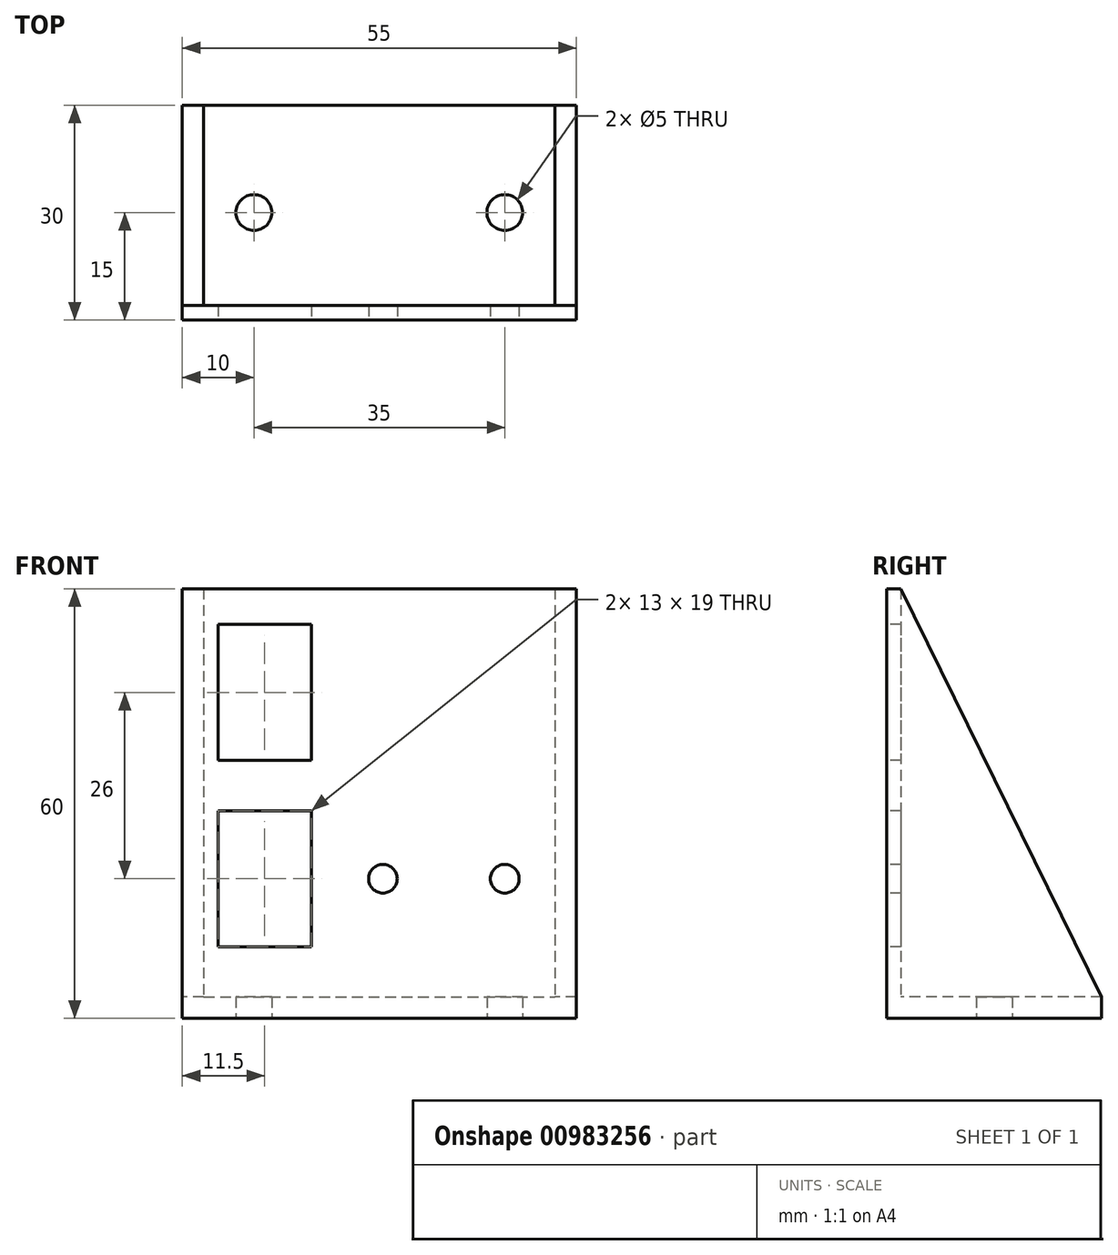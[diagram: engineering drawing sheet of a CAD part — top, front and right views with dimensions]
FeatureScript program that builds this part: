
annotation { "Feature Type Name" : "Feature", "Feature Type Description" : "" }
export const myFeature = defineFeature(function(context is Context, id is Id, definition is map)
    precondition{}
    {
        {
            var Q0;
            Q0=qCreatedBy(makeId("Top.planeOp"),FACE);
            var sketch = newSketch(context, id + "F0", { "sketchPlane" : qUnion([Q0])});
            skLineSegment(sketch, "E0.bottom", {"start": v(27.5, 15) * mm, "end": v(-27.5, 15) * mm});
            skLineSegment(sketch, "E0.top", {"start": v(27.5, -15) * mm, "end": v(-27.5, -15) * mm});
            skLineSegment(sketch, "E0.left", {"start": v(27.5, 15) * mm, "end": v(27.5, -15) * mm});
            skLineSegment(sketch, "E0.right", {"start": v(-27.5, 15) * mm, "end": v(-27.5, -15) * mm});
            skPoint(sketch, "E0.middle", {"position": v(0, 0) * mm});
            skLineSegment(sketch, "E1.bottom", {"start": v(-27.5, 15) * mm, "end": v(27.5, 15) * mm, "construction": true});
            skLineSegment(sketch, "E1.top", {"start": v(-27.5, 0) * mm, "end": v(27.5, 0) * mm, "construction": true});
            skLineSegment(sketch, "E1.left", {"start": v(-27.5, 15) * mm, "end": v(-27.5, 0) * mm, "construction": true});
            skLineSegment(sketch, "E1.right", {"start": v(27.5, 15) * mm, "end": v(27.5, 0) * mm, "construction": true});
            skLineSegment(sketch, "E2.bottom", {"start": v(-27.5, -15) * mm, "end": v(-17.5, -15) * mm, "construction": true});
            skLineSegment(sketch, "E2.top", {"start": v(-27.5, 15) * mm, "end": v(-17.5, 15) * mm, "construction": true});
            skLineSegment(sketch, "E2.left", {"start": v(-27.5, -15) * mm, "end": v(-27.5, 15) * mm, "construction": true});
            skLineSegment(sketch, "E2.right", {"start": v(-17.5, -15) * mm, "end": v(-17.5, 15) * mm, "construction": true});
            skLineSegment(sketch, "E3.bottom", {"start": v(27.5, 15) * mm, "end": v(17.5, 15) * mm, "construction": true});
            skLineSegment(sketch, "E3.top", {"start": v(27.5, -15) * mm, "end": v(17.5, -15) * mm, "construction": true});
            skLineSegment(sketch, "E3.left", {"start": v(27.5, 15) * mm, "end": v(27.5, -15) * mm, "construction": true});
            skLineSegment(sketch, "E3.right", {"start": v(17.5, 15) * mm, "end": v(17.5, -15) * mm, "construction": true});
            skCircle(sketch, "E4", {"center": v(-17.5, 0) * mm, "radius": 2.5 * mm});
            skCircle(sketch, "E5", {"center": v(17.5, 0) * mm, "radius": 2.5 * mm});
            skLineSegment(sketch, "E6.bottom", {"start": v(-27.5, 15) * mm, "end": v(-24.5, 15) * mm});
            skLineSegment(sketch, "E6.top", {"start": v(-27.5, -15) * mm, "end": v(-24.5, -15) * mm});
            skLineSegment(sketch, "E6.right", {"start": v(-24.5, 15) * mm, "end": v(-24.5, -15) * mm});
            skLineSegment(sketch, "E7.bottom", {"start": v(27.5, 15) * mm, "end": v(24.5, 15) * mm});
            skLineSegment(sketch, "E7.top", {"start": v(27.5, -15) * mm, "end": v(24.5, -15) * mm});
            skLineSegment(sketch, "E7.right", {"start": v(24.5, 15) * mm, "end": v(24.5, -15) * mm});
            skLineSegment(sketch, "E8.bottom", {"start": v(-27.5, -15) * mm, "end": v(27.5, -15) * mm});
            skLineSegment(sketch, "E8.top", {"start": v(-27.5, -13) * mm, "end": v(27.5, -13) * mm});
            skLineSegment(sketch, "E8.left", {"start": v(-27.5, -15) * mm, "end": v(-27.5, -13) * mm});
            skLineSegment(sketch, "E8.right", {"start": v(27.5, -15) * mm, "end": v(27.5, -13) * mm});
            skSolve(sketch);
        }
        {
            var Q0;
            Q0=makeQuery(id+"F0.imprint","IMPRINT",FACE,{"disambiguationData":[TD([[makeQuery(id+"F0.imprint","IMPRINT",EDGE,{"derivedFrom":sQuery(id+"F0.wireOp",EDGE,"E4")}),-1.0]])]});
            extrude(context, id + "F1", {"entities" : qUnion([Q0]), "depth" : 3 * mm, "offsetDistance" : 25 * mm});
        }
        {
            var Q0;
            {var subQ0=sQuery(id+"F0.wireOp",EDGE,"E0.right");var subQ1=sQuery(id+"F0.wireOp",EDGE,"E0.bottom");var subQ2=makeQuery(id+"F0.imprint","INTERSECT",VERTEX,{"derivedFrom":[subQ1,subQ0]});Q0=makeQuery(id+"F0.imprint","IMPRINT",FACE,{"disambiguationData":[TD([[makeQuery(id+"F0.imprint","IMPRINT",EDGE,{"disambiguationData":[TD([[subQ2,1.0]])],"derivedFrom":subQ1}),1.0]])]});}
            var Q1;
            {var subQ0=sQuery(id+"F0.wireOp",EDGE,"E0.right");var subQ1=sQuery(id+"F0.wireOp",EDGE,"E0.top");var subQ2=makeQuery(id+"F0.imprint","INTERSECT",VERTEX,{"derivedFrom":[subQ1,subQ0]});Q1=makeQuery(id+"F0.imprint","IMPRINT",FACE,{"disambiguationData":[TD([[makeQuery(id+"F0.imprint","IMPRINT",EDGE,{"disambiguationData":[TD([[subQ2,1.0]])],"derivedFrom":subQ1}),-1.0]])]});}
            var Q2;
            {var subQ0=sQuery(id+"F0.wireOp",EDGE,"E7.right");var subQ1=sQuery(id+"F0.wireOp",EDGE,"E0.top");var subQ2=makeQuery(id+"F0.imprint","INTERSECT",VERTEX,{"derivedFrom":[subQ1,subQ0]});Q2=makeQuery(id+"F0.imprint","IMPRINT",FACE,{"disambiguationData":[TD([[makeQuery(id+"F0.imprint","IMPRINT",EDGE,{"disambiguationData":[TD([[subQ2,-1.0]])],"derivedFrom":subQ1}),-1.0]])]});}
            var Q3;
            {var subQ0=sQuery(id+"F0.wireOp",EDGE,"E7.right");var subQ1=sQuery(id+"F0.wireOp",EDGE,"E0.top");var subQ2=makeQuery(id+"F0.imprint","INTERSECT",VERTEX,{"derivedFrom":[subQ1,subQ0]});Q3=makeQuery(id+"F0.imprint","IMPRINT",FACE,{"disambiguationData":[TD([[makeQuery(id+"F0.imprint","IMPRINT",EDGE,{"disambiguationData":[TD([[subQ2,1.0]])],"derivedFrom":subQ1}),-1.0]])]});}
            var Q4;
            {var subQ0=sQuery(id+"F0.wireOp",EDGE,"E7.right");var subQ1=sQuery(id+"F0.wireOp",EDGE,"E0.bottom");var subQ2=makeQuery(id+"F0.imprint","INTERSECT",VERTEX,{"derivedFrom":[subQ1,subQ0]});Q4=makeQuery(id+"F0.imprint","IMPRINT",FACE,{"disambiguationData":[TD([[makeQuery(id+"F0.imprint","IMPRINT",EDGE,{"disambiguationData":[TD([[subQ2,1.0]])],"derivedFrom":subQ1}),1.0]])]});}
            extrude(context, id + "F2", {"entities" : qUnion([Q0, Q1, Q2, Q3, Q4]), "operationType" : NewBodyOperationType.ADD, "depth" : 60 * mm, "offsetDistance" : 25 * mm});
        }
        {
            var Q0;
            Q0=makeQuery(id+"F2.opExtrude","SWEPT_FACE",FACE,{"disambiguationData":[OSD([sQuery(id+"F0.wireOp",EDGE,"E0.right")])]});
            var sketch = newSketch(context, id + "F3", { "sketchPlane" : qUnion([Q0])});
            skLineSegment(sketch, "E9.bottom", {"start": v(-15, 60) * mm, "end": v(13, 60) * mm});
            skLineSegment(sketch, "E9.left", {"start": v(-15, 60) * mm, "end": v(-15, 3) * mm});
            skLineSegment(sketch, "E10", {"start": v(-15, 3) * mm, "end": v(13, 60) * mm});
            skSolve(sketch);
        }
        {
            var Q0;
            Q0=makeQuery(id+"F3.imprint","IMPRINT",FACE,{"disambiguationData":[TD([[makeQuery(id+"F3.imprint","IMPRINT",EDGE,{"derivedFrom":sQuery(id+"F3.wireOp",EDGE,"E9.bottom")}),-1.0]])]});
            extrude(context, id + "F4", {"entities" : qUnion([Q0]), "operationType" : NewBodyOperationType.REMOVE, "oppositeDirection" : true, "depth" : 55 * mm, "offsetDistance" : 25 * mm});
        }
        {
            var Q0;
            Q0=makeQuery(id+"F2.opExtrude","SWEPT_FACE",FACE,{"disambiguationData":[OSD([sQuery(id+"F0.wireOp",EDGE,"E0.top")])]});
            var sketch = newSketch(context, id + "F5", { "sketchPlane" : qUnion([Q0])});
            skLineSegment(sketch, "E11.bottom", {"start": v(-27.5, 60) * mm, "end": v(-22.5, 60) * mm, "construction": true});
            skLineSegment(sketch, "E11.top", {"start": v(-27.5, 0) * mm, "end": v(-22.5, 0) * mm, "construction": true});
            skLineSegment(sketch, "E11.left", {"start": v(-27.5, 60) * mm, "end": v(-27.5, 0) * mm, "construction": true});
            skLineSegment(sketch, "E11.right", {"start": v(-22.5, 60) * mm, "end": v(-22.5, 0) * mm, "construction": true});
            skLineSegment(sketch, "E12.bottom", {"start": v(-27.5, 0) * mm, "end": v(27.5, 0) * mm, "construction": true});
            skLineSegment(sketch, "E12.left", {"start": v(-27.5, 0) * mm, "end": v(-27.5, 10) * mm, "construction": true});
            skLineSegment(sketch, "E13.top", {"start": v(-22.5, 29) * mm, "end": v(-9.5, 29) * mm});
            skLineSegment(sketch, "E13.left", {"start": v(-22.5, 10) * mm, "end": v(-22.5, 29) * mm});
            skLineSegment(sketch, "E13.right", {"start": v(-9.5, 10) * mm, "end": v(-9.5, 29) * mm});
            skLineSegment(sketch, "E14.left", {"start": v(-22.5, 29) * mm, "end": v(-22.5, 34) * mm, "construction": true});
            skLineSegment(sketch, "E14.right", {"start": v(27.5, 29) * mm, "end": v(27.5, 34) * mm, "construction": true});
            skLineSegment(sketch, "E15.left", {"start": v(-22.5, 34) * mm, "end": v(-22.5, 53) * mm});
            skLineSegment(sketch, "E16.bottom", {"start": v(-22.5, 29) * mm, "end": v(27.5, 29) * mm, "construction": true});
            skLineSegment(sketch, "E16.top", {"start": v(-22.5, 36) * mm, "end": v(27.5, 36) * mm, "construction": true});
            skLineSegment(sketch, "E16.left", {"start": v(-22.5, 29) * mm, "end": v(-22.5, 36) * mm, "construction": true});
            skLineSegment(sketch, "E16.right", {"start": v(27.5, 29) * mm, "end": v(27.5, 36) * mm, "construction": true});
            skLineSegment(sketch, "E17.bottom", {"start": v(-22.5, 36) * mm, "end": v(-9.5, 36) * mm});
            skLineSegment(sketch, "E17.top", {"start": v(-22.5, 55) * mm, "end": v(-9.5, 55) * mm});
            skLineSegment(sketch, "E17.left", {"start": v(-22.5, 36) * mm, "end": v(-22.5, 55) * mm});
            skLineSegment(sketch, "E17.right", {"start": v(-9.5, 36) * mm, "end": v(-9.5, 55) * mm});
            skLineSegment(sketch, "E18.left", {"start": v(-22.5, 10) * mm, "end": v(-22.5, 19.5) * mm, "construction": true});
            skLineSegment(sketch, "E19.left", {"start": v(-9.5, 19.5) * mm, "end": v(-9.5, 10) * mm, "construction": true});
            skLineSegment(sketch, "E20.left", {"start": v(-9.5, 10) * mm, "end": v(-9.5, 18.54) * mm, "construction": true});
            skLineSegment(sketch, "E21", {"start": v(-22.5, 10) * mm, "end": v(-9.5, 10) * mm});
            skLineSegment(sketch, "E22.top", {"start": v(-27.5, 10) * mm, "end": v(27.5, 10) * mm, "construction": true});
            skLineSegment(sketch, "E22.right", {"start": v(27.5, 0) * mm, "end": v(27.5, 10) * mm, "construction": true});
            skLineSegment(sketch, "E23.bottom", {"start": v(-9.5, 10) * mm, "end": v(0.5, 10) * mm, "construction": true});
            skLineSegment(sketch, "E23.top", {"start": v(-9.5, 19.5) * mm, "end": v(0.5, 19.5) * mm, "construction": true});
            skLineSegment(sketch, "E23.left", {"start": v(-9.5, 10) * mm, "end": v(-9.5, 19.5) * mm, "construction": true});
            skLineSegment(sketch, "E23.right", {"start": v(0.5, 10) * mm, "end": v(0.5, 19.5) * mm, "construction": true});
            skLineSegment(sketch, "E24.bottom", {"start": v(27.5, 10) * mm, "end": v(17.5, 10) * mm, "construction": true});
            skLineSegment(sketch, "E24.top", {"start": v(27.5, 19.5) * mm, "end": v(17.5, 19.5) * mm, "construction": true});
            skLineSegment(sketch, "E24.left", {"start": v(27.5, 10) * mm, "end": v(27.5, 19.5) * mm, "construction": true});
            skLineSegment(sketch, "E24.right", {"start": v(17.5, 10) * mm, "end": v(17.5, 19.5) * mm, "construction": true});
            skCircle(sketch, "E25", {"center": v(0.5, 19.5) * mm, "radius": 7 * mm, "construction": true});
            skCircle(sketch, "E26", {"center": v(17.5, 19.5) * mm, "radius": 7 * mm, "construction": true});
            skCircle(sketch, "E27", {"center": v(0.5, 19.5) * mm, "radius": 2 * mm});
            skCircle(sketch, "E28", {"center": v(17.5, 19.5) * mm, "radius": 2 * mm});
            skSolve(sketch);
        }
        {
            var Q0;
            {var subQ3=sQuery(id+"F5.wireOp",EDGE,"E17.bottom");Q0=makeQuery(id+"F5.imprint","IMPRINT",FACE,{"disambiguationData":[TD([[makeQuery(id+"F5.imprint","IMPRINT",EDGE,{"derivedFrom":subQ3}),1.0]])]});}
            var Q1;
            Q1=makeQuery(id+"F5.imprint","IMPRINT",FACE,{"disambiguationData":[TD([[makeQuery(id+"F5.imprint","IMPRINT",EDGE,{"derivedFrom":sQuery(id+"F5.wireOp",EDGE,"E13.bottom")}),1.0]])]});
            var Q2;
            Q2=makeQuery(id+"F5.imprint","IMPRINT",FACE,{"disambiguationData":[TD([[makeQuery(id+"F5.imprint","IMPRINT",EDGE,{"derivedFrom":sQuery(id+"F5.wireOp",EDGE,"E13.top")}),-1.0]])]});
            var Q3;
            Q3=makeQuery(id+"F5.imprint","IMPRINT",FACE,{"disambiguationData":[TD([[makeQuery(id+"F5.imprint","IMPRINT",EDGE,{"derivedFrom":sQuery(id+"F5.wireOp",EDGE,"E27")}),1.0]])]});
            var Q4;
            Q4=makeQuery(id+"F5.imprint","IMPRINT",FACE,{"disambiguationData":[TD([[makeQuery(id+"F5.imprint","IMPRINT",EDGE,{"derivedFrom":sQuery(id+"F5.wireOp",EDGE,"E28")}),1.0]])]});
            extrude(context, id + "F6", {"entities" : qUnion([Q0, Q1, Q2, Q3, Q4]), "operationType" : NewBodyOperationType.REMOVE, "oppositeDirection" : true, "depth" : 25 * mm, "offsetDistance" : 25 * mm});
        }
    });
